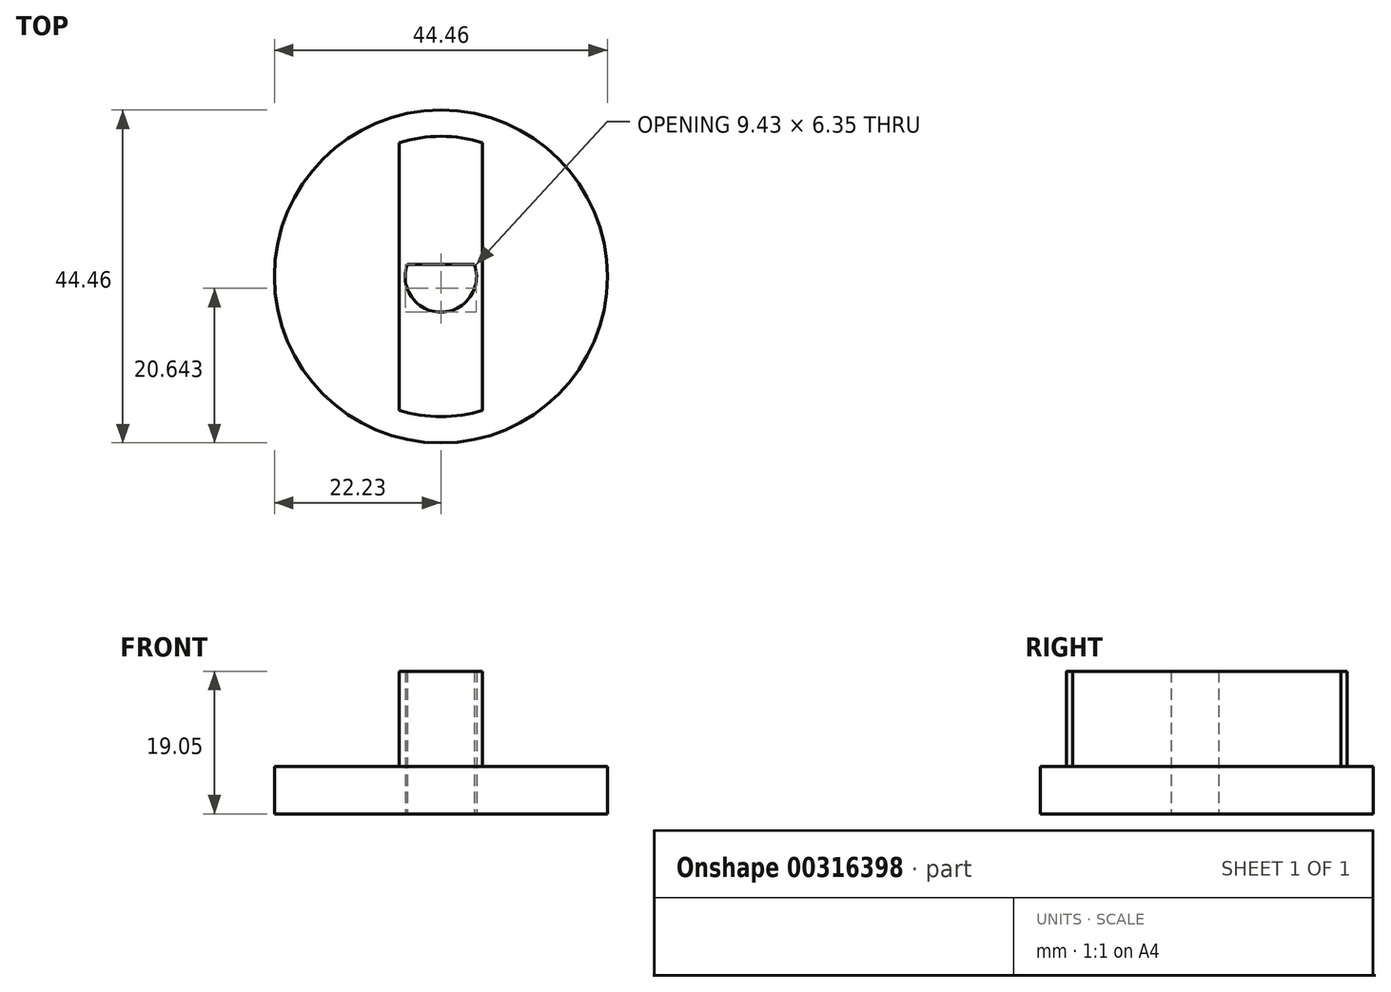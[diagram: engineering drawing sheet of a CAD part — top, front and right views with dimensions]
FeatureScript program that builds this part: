
annotation { "Feature Type Name" : "Feature", "Feature Type Description" : "" }
export const myFeature = defineFeature(function(context is Context, id is Id, definition is map)
    precondition{}
    {
        {
            var Q0;
            Q0=qCreatedBy(makeId("Top.planeOp"),FACE);
            var sketch = newSketch(context, id + "F0", { "sketchPlane" : qUnion([Q0])});
            skCircle(sketch, "E0", {"center": v(0, 0) * mm, "radius": 22.23 * mm});
            skArc(sketch, "E1", {"start": v(-4.5, 1.59) * mm, "mid": v(0, -4.76) * mm, "end": v(4.5, 1.59) * mm});
            skLineSegment(sketch, "E2", {"start": v(4.5, 1.59) * mm, "end": v(4.5, 1.59) * mm});
            skLineSegment(sketch, "E3", {"start": v(4.5, 1.59) * mm, "end": v(-4.5, 1.59) * mm});
            skSolve(sketch);
        }
        {
            var Q0;
            Q0=makeQuery(id+"F0.imprint","IMPRINT",FACE,{"disambiguationData":[TD([[makeQuery(id+"F0.imprint","IMPRINT",EDGE,{"derivedFrom":sQuery(id+"F0.wireOp",EDGE,"E0")}),1.0]])]});
            extrude(context, id + "F1", {"entities" : qUnion([Q0]), "depth" : 6.35 * mm});
        }
        {
            var Q0;
            Q0=makeQuery(id+"F1.opExtrude","CAP_FACE",FACE,{"disambiguationData":[OSD([sQuery(id+"F0.wireOp",EDGE,"E0"),sQuery(id+"F0.wireOp",EDGE,"E1"),sQuery(id+"F0.wireOp",EDGE,"E3")])],"isStart":false});
            var sketch = newSketch(context, id + "F2", { "sketchPlane" : qUnion([Q0])});
            skArc(sketch, "E4", {"start": v(-5.55, -17.88) * mm, "mid": v(0, -18.73) * mm, "end": v(5.55, -17.88) * mm});
            skLineSegment(sketch, "E5", {"start": v(-5.55, 17.88) * mm, "end": v(-5.55, -17.88) * mm});
            skLineSegment(sketch, "E6", {"start": v(5.55, 17.88) * mm, "end": v(5.55, -17.88) * mm});
            skArc(sketch, "E7.trimOffspring", {"start": v(5.55, 17.88) * mm, "mid": v(0, 18.73) * mm, "end": v(-5.55, 17.88) * mm});
            skSolve(sketch);
        }
        {
            var Q0;
            Q0=makeQuery(id+"F2.imprint","IMPRINT",FACE,{"disambiguationData":[TD([[makeQuery(id+"F2.imprint","IMPRINT",EDGE,{"derivedFrom":sQuery(id+"F2.wireOp",EDGE,"E4")}),1.0]])]});
            extrude(context, id + "F3", {"entities" : qUnion([Q0]), "operationType" : NewBodyOperationType.ADD, "depth" : 12.7 * mm});
        }
    });
